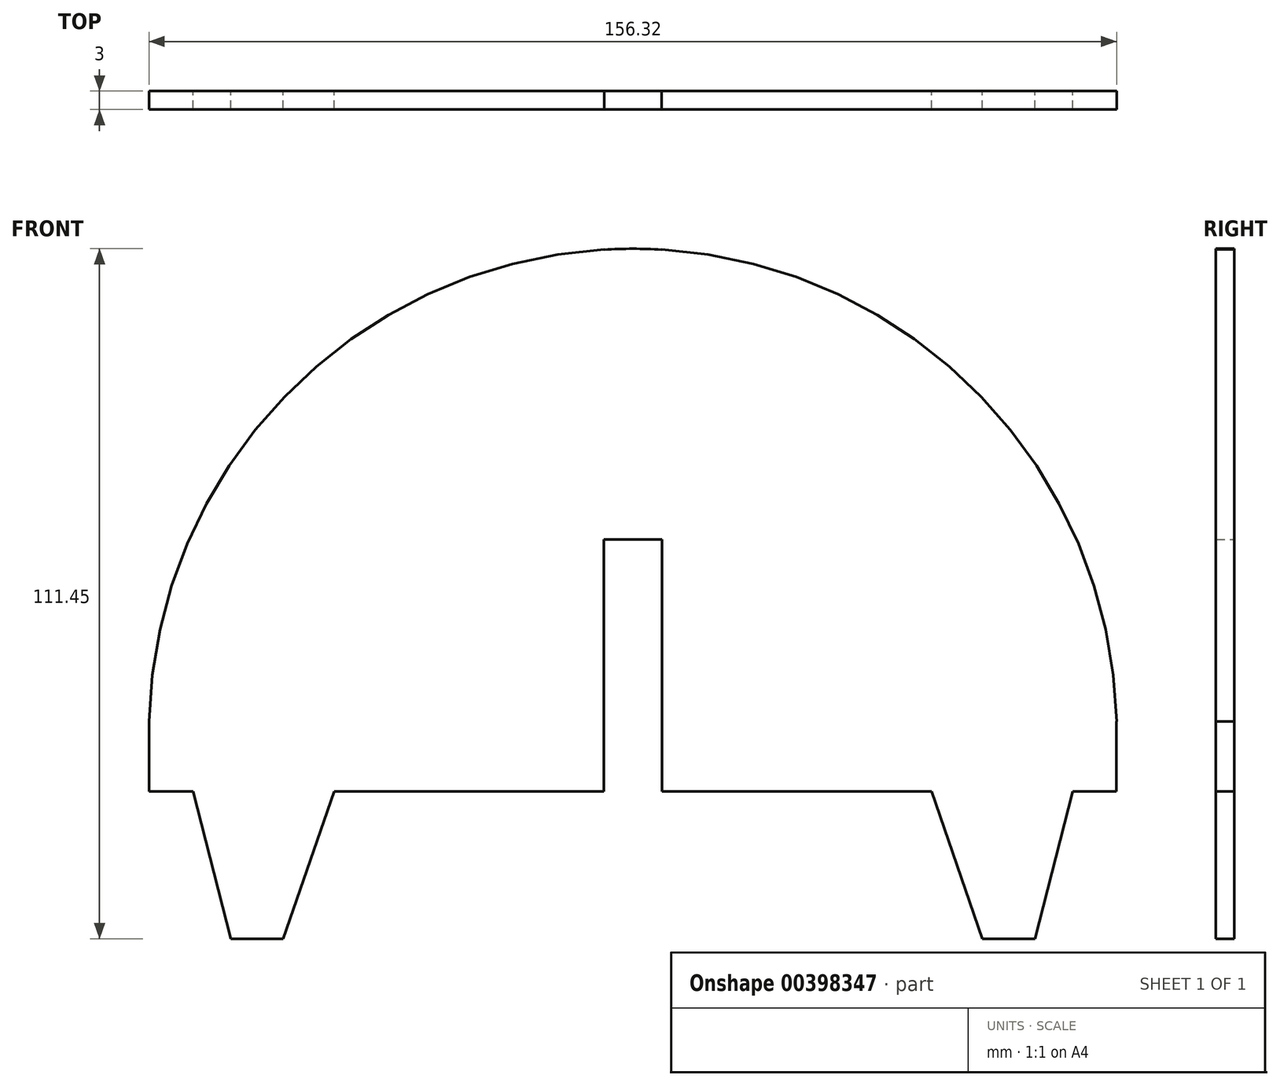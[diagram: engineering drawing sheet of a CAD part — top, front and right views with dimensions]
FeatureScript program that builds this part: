
annotation { "Feature Type Name" : "Feature", "Feature Type Description" : "" }
export const myFeature = defineFeature(function(context is Context, id is Id, definition is map)
    precondition{}
    {
        {
            var Q0;
            Q0=qCreatedBy(makeId("Front.planeOp"),FACE);
            var sketch = newSketch(context, id + "F0", { "sketchPlane" : qUnion([Q0])});
            skLineSegment(sketch, "E0.right", {"start": v(4.7, 76.06) * mm, "end": v(4.7, 0) * mm});
            skArc(sketch, "E1", {"start": v(78.16, 0) * mm, "mid": v(56.28, 52.48) * mm, "end": v(4.63, 76.25) * mm});
            skLineSegment(sketch, "E2", {"start": v(-78.16, 0) * mm, "end": v(-78.15, 0) * mm});
            skLineSegment(sketch, "E3", {"start": v(-4.92, 76.06) * mm, "end": v(-4.86, 76.24) * mm});
            skLineSegment(sketch, "E4", {"start": v(4.63, 76.25) * mm, "end": v(4.7, 76.06) * mm});
            skPoint(sketch, "E5.orphan", {"position": v(0, 89.26) * mm});
            skArc(sketch, "E6", {"start": v(78.15, 0) * mm, "mid": v(54.64, 54.12) * mm, "end": v(0, 76.38) * mm});
            skLineSegment(sketch, "E7.top", {"start": v(4.7, -11.3) * mm, "end": v(78.14, -11.3) * mm});
            skLineSegment(sketch, "E7.right", {"start": v(78.14, 0) * mm, "end": v(78.14, -11.3) * mm});
            skLineSegment(sketch, "E8.right", {"start": v(4.7, 0) * mm, "end": v(4.7, -11.3) * mm});
            skLineSegment(sketch, "E9.trimOffspring", {"start": v(78.14, 0) * mm, "end": v(78.16, 0) * mm});
            skLineSegment(sketch, "E10", {"start": v(0, 29.42) * mm, "end": v(4.7, 29.42) * mm});
            skPoint(sketch, "E10.endSnap0", {"position": v(4.7, 38.03) * mm});
            skLineSegment(sketch, "E11", {"start": v(48.25, -11.3) * mm, "end": v(56.49, -35.07) * mm});
            skLineSegment(sketch, "E12", {"start": v(56.49, -35.07) * mm, "end": v(64.96, -35.07) * mm});
            skLineSegment(sketch, "E13", {"start": v(64.96, -35.07) * mm, "end": v(71.08, -11.3) * mm});
            skLineSegment(sketch, "E14.MirrorCS", {"start": v(-4.63, 76.25) * mm, "end": v(-4.7, 76.06) * mm});
            skLineSegment(sketch, "E15.MirrorCS", {"start": v(4.92, 76.06) * mm, "end": v(4.86, 76.24) * mm});
            skArc(sketch, "E16.MirrorCS", {"start": v(-78.16, 0) * mm, "mid": v(-56.28, 52.48) * mm, "end": v(-4.63, 76.25) * mm});
            skLineSegment(sketch, "E17.MirrorCS", {"start": v(-4.7, 0) * mm, "end": v(-4.7, -11.3) * mm});
            skLineSegment(sketch, "E18.MirrorCS", {"start": v(-4.7, -11.3) * mm, "end": v(-78.14, -11.3) * mm});
            skArc(sketch, "E19.MirrorCS", {"start": v(-78.15, 0) * mm, "mid": v(-54.64, 54.12) * mm, "end": v(0, 76.38) * mm});
            skLineSegment(sketch, "E20.MirrorCS", {"start": v(-78.14, 0) * mm, "end": v(-78.14, -11.3) * mm});
            skLineSegment(sketch, "E21.MirrorCS", {"start": v(-64.96, -35.07) * mm, "end": v(-71.08, -11.3) * mm});
            skPoint(sketch, "E22.MirrorP", {"position": v(-4.7, 38.03) * mm});
            skLineSegment(sketch, "E23.MirrorCS", {"start": v(-78.14, 0) * mm, "end": v(-78.16, 0) * mm});
            skLineSegment(sketch, "E24.MirrorCS", {"start": v(-48.25, -11.3) * mm, "end": v(-56.49, -35.07) * mm});
            skLineSegment(sketch, "E25.MirrorCS", {"start": v(-56.49, -35.07) * mm, "end": v(-64.96, -35.07) * mm});
            skLineSegment(sketch, "E26.MirrorCS", {"start": v(-4.7, 76.06) * mm, "end": v(-4.7, 0) * mm});
            skPoint(sketch, "E27.MirrorCS.end.orphan", {"position": v(-4.7, 29.42) * mm});
            skPoint(sketch, "E27.MirrorCS.start.orphan", {"position": v(0, 29.42) * mm});
            skLineSegment(sketch, "E28", {"start": v(-4.7, 29.42) * mm, "end": v(0, 29.42) * mm});
            skPoint(sketch, "E29.MirrorCS.start.orphan", {"position": v(0, -11.3) * mm});
            skSolve(sketch);
        }
        {
            var Q0;
            Q0 = qSketchRegion(id + "F0", true);
            extrude(context, id + "F1", {"entities" : qUnion([Q0]), "depth" : 3 * mm});
        }
    });
